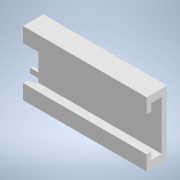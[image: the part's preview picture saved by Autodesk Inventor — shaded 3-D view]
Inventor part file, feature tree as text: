
AUTODESK INVENTOR PART (.ipt)
format: ipt  version: 2021 (Build 250183000, 183)  size: 144,384 bytes
history: native  units: in
note: dims shown in document units (in); Inventor stores cm internally (conversion verified against a paired STEP export)
features: extrude x4, sketch x4
ambient origin geometry x8: Origin, YZ Plane, XZ Plane, XY Plane, X Axis, Y Axis, Z Axis, Center Point
bodies: Solid1 (feature_tree)
feature tree (8):
  extrude  "Extrusion1"  Depth=5.1181in
  extrude  "Extrusion2"  Depth=0.5906in
  extrude  "Extrusion3"  Depth=0.8268in TaperAngle=0.0deg
  extrude  "Extrusion4"  Depth=1.1811in
  sketch  "Sketch1"  dims[d0=9.8425in d1=5.1181in]
  sketch  "Sketch2"  dims[d2=0.3937in d3=0.0in d4=0.5906in]
  sketch  "Sketch3"  dims[d5=0.5906in d6=0.8268in d7=0.0in]
  sketch  "Sketch4"  dims[d8=1.1811in d9=1.1811in d10=0.3937in d11=0.0in d12=0.1969in d13=0.3937in d14=0.3937in d15=0.0in d16=0.0in d17=0.7874in d18=0.0in d19=0.0197in d20=0.0344in d21=0.0197in d22=0.0344in]
